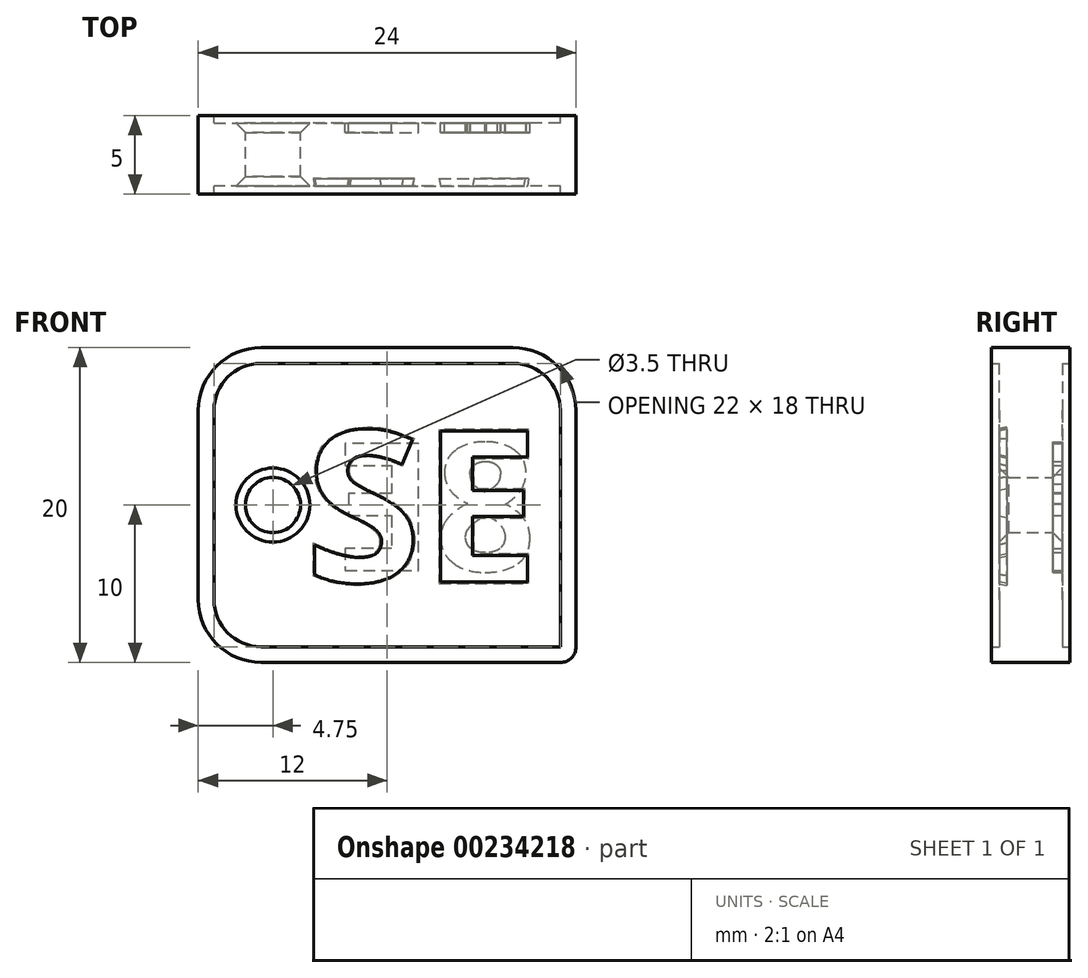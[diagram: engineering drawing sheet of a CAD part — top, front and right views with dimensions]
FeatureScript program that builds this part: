
annotation { "Feature Type Name" : "Feature", "Feature Type Description" : "" }
export const myFeature = defineFeature(function(context is Context, id is Id, definition is map)
    precondition{}
    {
        {
            var Q0;
            Q0=qCreatedBy(makeId("Front.planeOp"),FACE);
            var sketch = newSketch(context, id + "F0", { "sketchPlane" : qUnion([Q0])});
            skLineSegment(sketch, "E0.bottom", {"start": v(12, -10) * mm, "end": v(-12, -10) * mm});
            skLineSegment(sketch, "E0.top", {"start": v(12, 10) * mm, "end": v(-12, 10) * mm});
            skLineSegment(sketch, "E0.left", {"start": v(12, -10) * mm, "end": v(12, 10) * mm});
            skLineSegment(sketch, "E0.right", {"start": v(-12, -10) * mm, "end": v(-12, 10) * mm});
            skPoint(sketch, "E0.middle", {"position": v(0, 0) * mm});
            skCircle(sketch, "E1", {"center": v(-7.25, 0) * mm, "radius": 1.75 * mm});
            skSolve(sketch);
        }
        {
            var Q0;
            Q0 = qSketchRegion(id + "F0", true);
            extrude(context, id + "F1", {"entities" : qUnion([Q0]), "endBound" : BoundingType.SYMMETRIC, "depth" : 4 * mm});
        }
        {
            var Q0;
            Q0=makeQuery(id+"F1.opExtrude","SWEPT_EDGE",EDGE,{"disambiguationData":[OSD([sQuery(id+"F0.wireOp",EDGE,"E0.top"),sQuery(id+"F0.wireOp",EDGE,"E0.right")])]});
            var Q1;
            Q1=makeQuery(id+"F1.opExtrude","SWEPT_EDGE",EDGE,{"disambiguationData":[OSD([sQuery(id+"F0.wireOp",EDGE,"E0.top"),sQuery(id+"F0.wireOp",EDGE,"E0.left")])]});
            var Q2;
            Q2=makeQuery(id+"F1.opExtrude","SWEPT_EDGE",EDGE,{"disambiguationData":[OSD([sQuery(id+"F0.wireOp",EDGE,"E0.bottom"),sQuery(id+"F0.wireOp",EDGE,"E0.right")])]});
            fillet(context, id + "F2", {"entities" : qUnion([Q0, Q1, Q2]), "radius" : 4 * mm, "tangentPropagation" : true, "allowEdgeOverflow" : false});
        }
        {
            var Q0;
            Q0=makeQuery(id+"F1.opExtrude","SWEPT_EDGE",EDGE,{"disambiguationData":[OSD([sQuery(id+"F0.wireOp",EDGE,"E0.bottom"),sQuery(id+"F0.wireOp",EDGE,"E0.left")])]});
            fillet(context, id + "F3", {"entities" : qUnion([Q0]), "radius" : 1 * mm, "tangentPropagation" : true, "allowEdgeOverflow" : false});
        }
        {
            var Q0;
            Q0=qCreatedBy(makeId("Front.planeOp"),FACE);
            var sketch = newSketch(context, id + "F4", { "sketchPlane" : qUnion([Q0])});
            skArc(sketch, "E2.0", {"start": v(-11, -6) * mm, "mid": v(-10.12, -8.12) * mm, "end": v(-8, -9) * mm});
            skLineSegment(sketch, "E2.1", {"start": v(-11, 6) * mm, "end": v(-11, -6) * mm});
            skLineSegment(sketch, "E2.2", {"start": v(11, -9) * mm, "end": v(11, 6) * mm});
            skArc(sketch, "E2.3", {"start": v(11, 6) * mm, "mid": v(10.12, 8.12) * mm, "end": v(8, 9) * mm});
            skLineSegment(sketch, "E2.4", {"start": v(8, 9) * mm, "end": v(-8, 9) * mm});
            skLineSegment(sketch, "E2.5", {"start": v(-8, -9) * mm, "end": v(11, -9) * mm});
            skArc(sketch, "E2.6", {"start": v(-8, 9) * mm, "mid": v(-10.12, 8.12) * mm, "end": v(-11, 6) * mm});
            skArc(sketch, "E3.0", {"start": v(-12, -6) * mm, "mid": v(-10.83, -8.83) * mm, "end": v(-8, -10) * mm});
            skLineSegment(sketch, "E3.1", {"start": v(-12, 6) * mm, "end": v(-12, -6) * mm});
            skLineSegment(sketch, "E3.2", {"start": v(-8, -10) * mm, "end": v(11, -10) * mm});
            skArc(sketch, "E3.3", {"start": v(-8, 10) * mm, "mid": v(-10.83, 8.83) * mm, "end": v(-12, 6) * mm});
            skArc(sketch, "E3.4", {"start": v(11, -10) * mm, "mid": v(11.7, -9.7) * mm, "end": v(12, -9) * mm});
            skLineSegment(sketch, "E3.5", {"start": v(12, -9) * mm, "end": v(12, 6) * mm});
            skArc(sketch, "E3.6", {"start": v(12, 6) * mm, "mid": v(10.83, 8.83) * mm, "end": v(8, 10) * mm});
            skLineSegment(sketch, "E3.7", {"start": v(8, 10) * mm, "end": v(-8, 10) * mm});
            skSolve(sketch);
        }
        {
            var Q0;
            Q0 = qSketchRegion(id + "F4", true);
            extrude(context, id + "F5", {"entities" : qUnion([Q0]), "operationType" : NewBodyOperationType.ADD, "endBound" : BoundingType.SYMMETRIC, "depth" : 5 * mm});
        }
        {
            var Q0;
            Q0=makeQuery(id+"F1.opExtrude","CAP_FACE",FACE,{"disambiguationData":[OSD([sQuery(id+"F0.wireOp",EDGE,"E0.bottom"),sQuery(id+"F0.wireOp",EDGE,"E0.top"),sQuery(id+"F0.wireOp",EDGE,"E0.left"),sQuery(id+"F0.wireOp",EDGE,"E0.right"),sQuery(id+"F0.wireOp",EDGE,"E1")])],"isStart":false});
            var sketch = newSketch(context, id + "F6", { "sketchPlane" : qUnion([Q0])});
            skText(sketch, "E4", { "text": "SE", "fontName": "OpenSans-Bold.ttf"});
            const initialGuessF6  = {"E4": [-0.00522, -0.00488, 1, 0, 0.00967]};
            skSetInitialGuess(sketch, initialGuessF6);
            skSolve(sketch);
        }
        {
            var Q0;
            Q0 = qSketchRegion(id + "F6", true);
            extrude(context, id + "F7", {"entities" : qUnion([Q0]), "operationType" : NewBodyOperationType.REMOVE, "oppositeDirection" : true, "depth" : 0.5 * mm, "hasDraft" : true, "draftAngle" : 10 * degree});
        }
        {
            var Q0;
            Q0=makeQuery(id+"F1.opExtrude","CAP_EDGE",EDGE,{"disambiguationData":[OSD([sQuery(id+"F0.wireOp",EDGE,"E1")])],"isStart":false});
            var Q1;
            Q1=makeQuery(id+"F1.opExtrude","CAP_EDGE",EDGE,{"disambiguationData":[OSD([sQuery(id+"F0.wireOp",EDGE,"E1")])],"isStart":true});
            chamfer(context, id + "F8", {"entities" : qUnion([Q0, Q1]), "width" : .6 * mm, "tangentPropagation" : true});
        }
        {
            var Q0;
            Q0=makeQuery(id+"F1.opExtrude","CAP_FACE",FACE,{"disambiguationData":[OSD([sQuery(id+"F0.wireOp",EDGE,"E0.bottom"),sQuery(id+"F0.wireOp",EDGE,"E0.top"),sQuery(id+"F0.wireOp",EDGE,"E0.left"),sQuery(id+"F0.wireOp",EDGE,"E0.right"),sQuery(id+"F0.wireOp",EDGE,"E1")])],"isStart":true});
            var sketch = newSketch(context, id + "F9", { "sketchPlane" : qUnion([Q0])});
            skText(sketch, "E5", { "text": "8E", "fontName": "OpenSans-Bold.ttf"});
            const initialGuessF9  = {"E5": [-0.00947, -0.00417, 1, 0, 0.00815]};
            skSetInitialGuess(sketch, initialGuessF9);
            skSolve(sketch);
        }
        {
            var Q0;
            Q0 = qSketchRegion(id + "F9", true);
            extrude(context, id + "F10", {"entities" : qUnion([Q0]), "operationType" : NewBodyOperationType.REMOVE, "oppositeDirection" : true, "depth" : 0.6 * mm});
        }
    });
